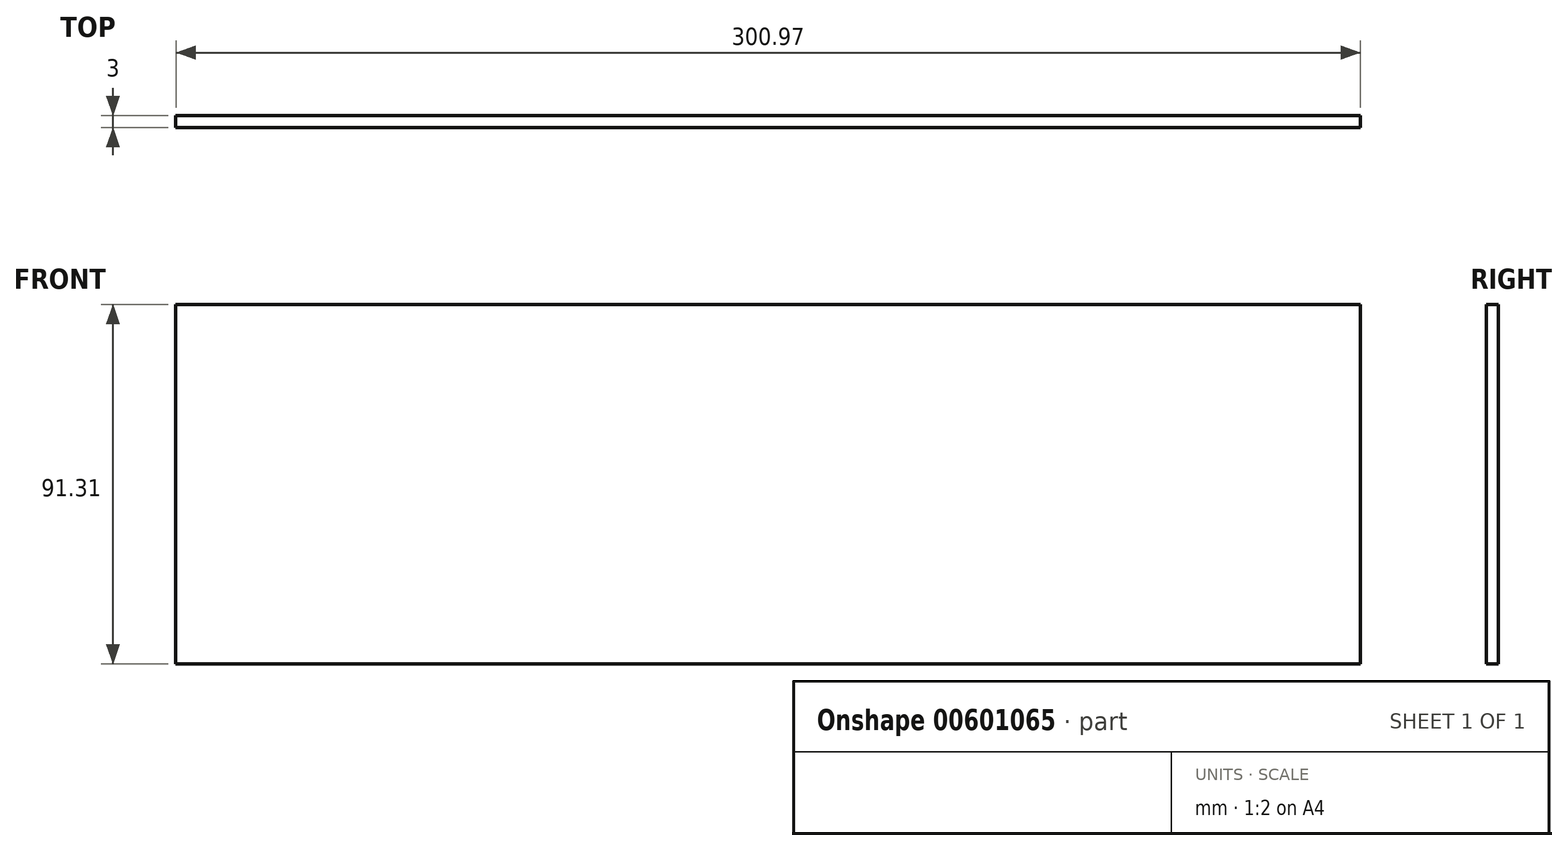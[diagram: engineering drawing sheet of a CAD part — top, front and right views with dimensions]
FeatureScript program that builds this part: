
annotation { "Feature Type Name" : "Feature", "Feature Type Description" : "" }
export const myFeature = defineFeature(function(context is Context, id is Id, definition is map)
    precondition{}
    {
        {
            var Q0;
            Q0=qCreatedBy(makeId("Front.planeOp"),FACE);
            var sketch = newSketch(context, id + "F0", { "sketchPlane" : qUnion([Q0])});
            skLineSegment(sketch, "E0.bottom", {"start": v(-84.38, 102.49) * mm, "end": v(216.6, 102.49) * mm});
            skLineSegment(sketch, "E0.top", {"start": v(-84.38, 11.18) * mm, "end": v(216.6, 11.18) * mm});
            skLineSegment(sketch, "E0.left", {"start": v(-84.38, 102.49) * mm, "end": v(-84.38, 11.18) * mm});
            skLineSegment(sketch, "E0.right", {"start": v(216.6, 102.49) * mm, "end": v(216.6, 11.18) * mm});
            skSolve(sketch);
        }
        {
            var Q0;
            Q0 = qSketchRegion(id + "F0", true);
            extrude(context, id + "F1", {"entities" : qUnion([Q0]), "depth" : 3 * mm, "offsetDistance" : 25 * mm});
        }
    });
